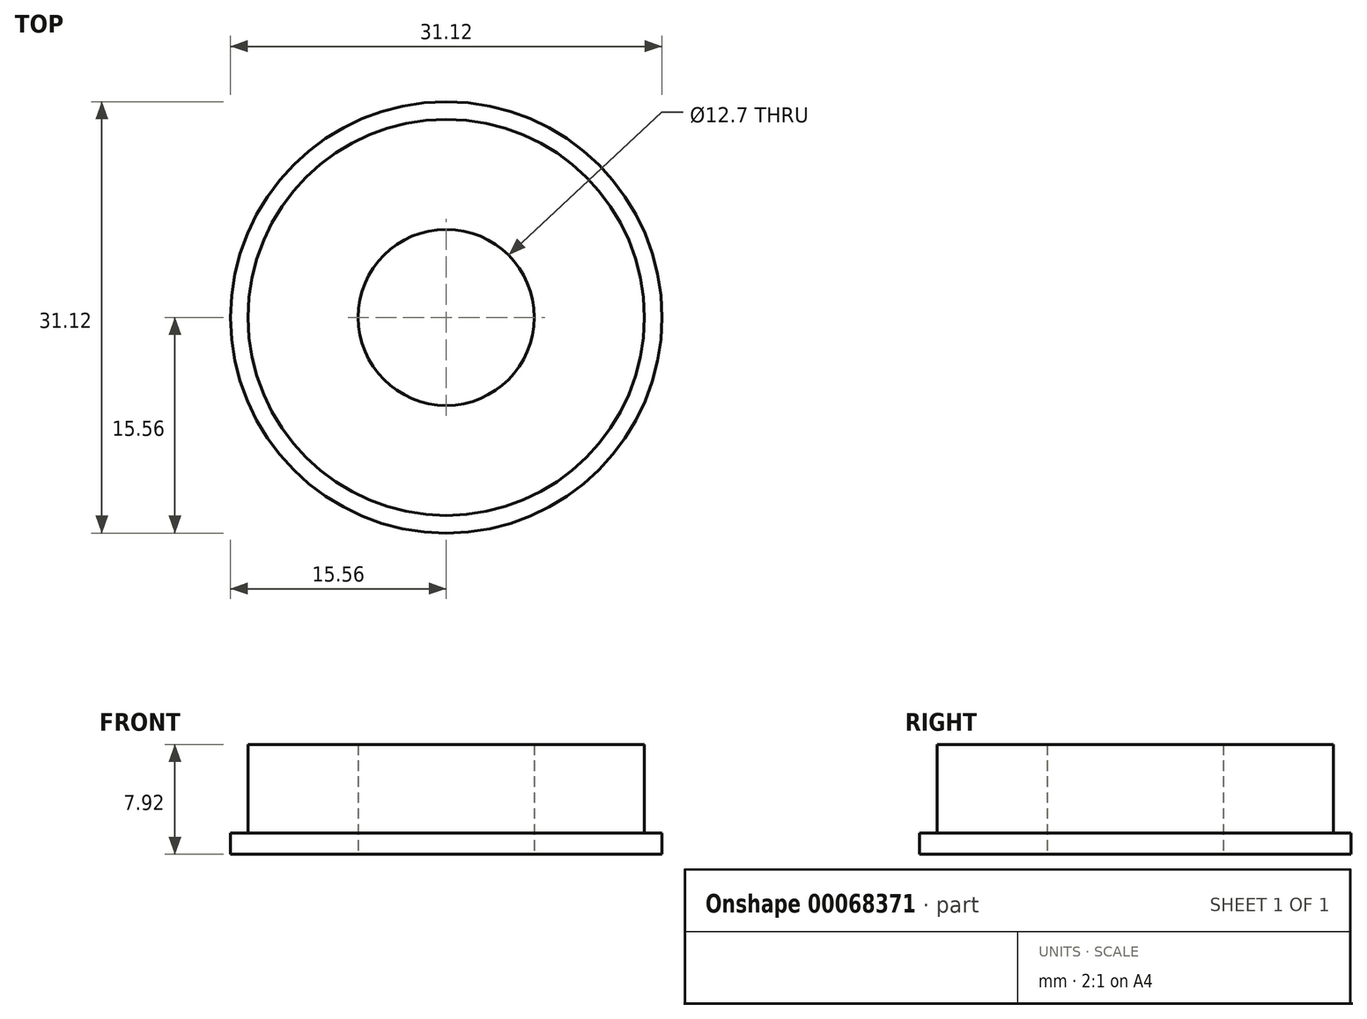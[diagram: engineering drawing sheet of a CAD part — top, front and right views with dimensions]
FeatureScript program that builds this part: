
annotation { "Feature Type Name" : "Feature", "Feature Type Description" : "" }
export const myFeature = defineFeature(function(context is Context, id is Id, definition is map)
    precondition{}
    {
        {
            var Q0;
            Q0=qCreatedBy(makeId("Top.planeOp"),FACE);
            var sketch = newSketch(context, id + "F0", { "sketchPlane" : qUnion([Q0])});
            skCircle(sketch, "E0", {"center": v(0, 0) * mm, "radius": 14.29 * mm});
            skSolve(sketch);
        }
        {
            var Q0;
            Q0=qCreatedBy(makeId("Top.planeOp"),FACE);
            var sketch = newSketch(context, id + "F1", { "sketchPlane" : qUnion([Q0])});
            skCircle(sketch, "E1", {"center": v(0, 0) * mm, "radius": 15.56 * mm});
            skSolve(sketch);
        }
        {
            var Q0;
            Q0=qCreatedBy(makeId("Top.planeOp"),FACE);
            var sketch = newSketch(context, id + "F2", { "sketchPlane" : qUnion([Q0])});
            skCircle(sketch, "E2", {"center": v(0, 0) * mm, "radius": 6.35 * mm});
            skSolve(sketch);
        }
        {
            var Q0;
            Q0 = qSketchRegion(id + "F0", true);
            extrude(context, id + "F3", {"entities" : qUnion([Q0]), "depth" : 7.92 * mm});
        }
        {
            var Q0;
            Q0 = qSketchRegion(id + "F1", true);
            extrude(context, id + "F4", {"entities" : qUnion([Q0]), "operationType" : NewBodyOperationType.ADD, "depth" : 1.52 * mm});
        }
        {
            var Q0;
            Q0 = qSketchRegion(id + "F2", true);
            extrude(context, id + "F5", {"entities" : qUnion([Q0]), "operationType" : NewBodyOperationType.REMOVE, "depth" : 25.4 * mm});
        }
    });
